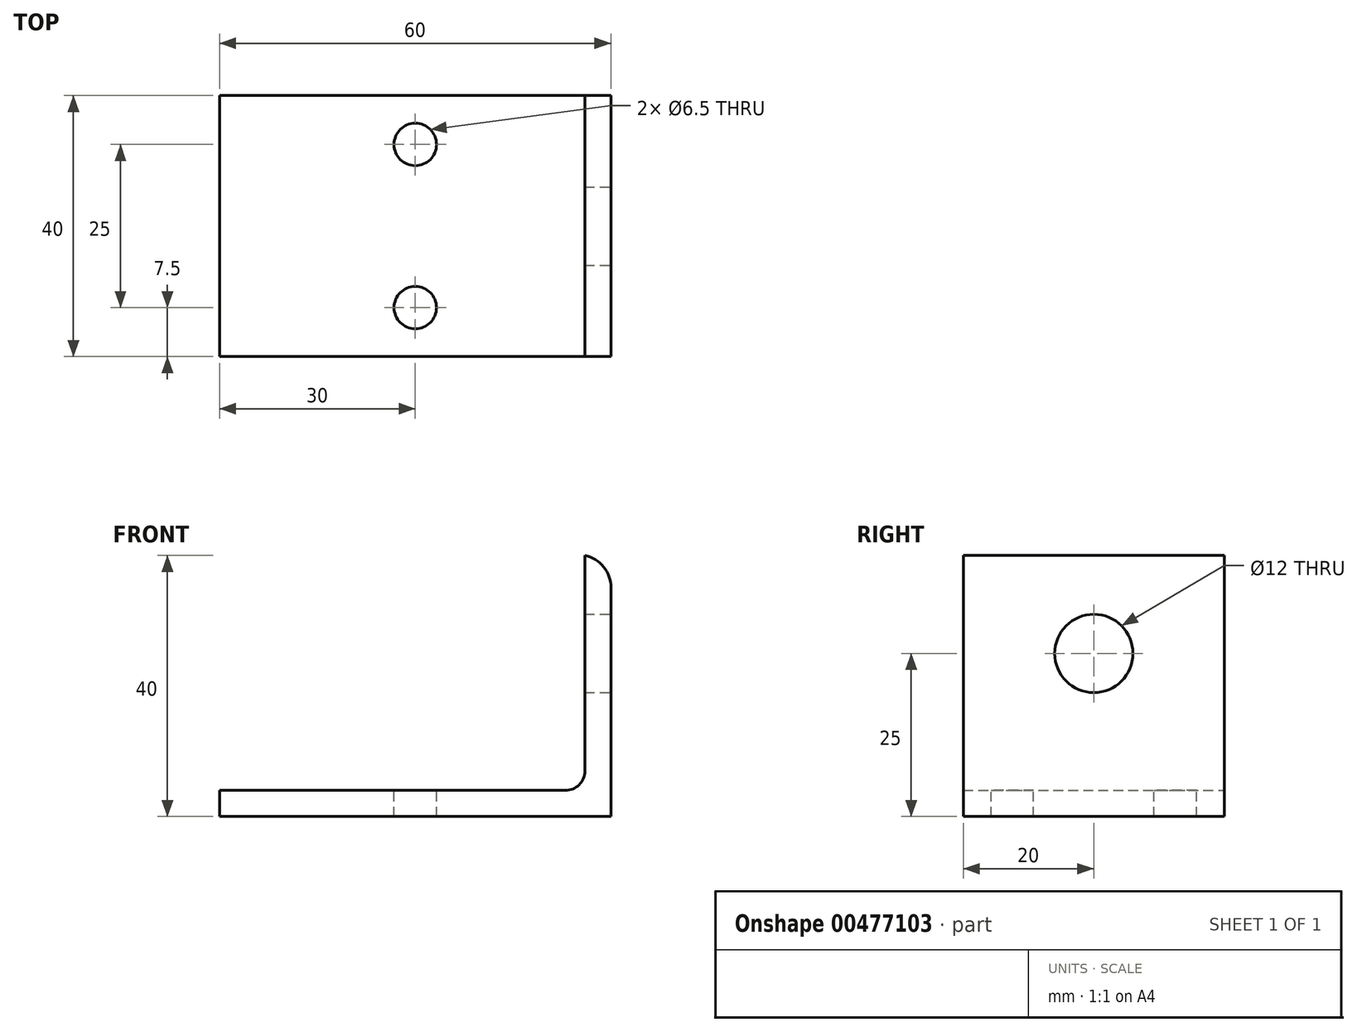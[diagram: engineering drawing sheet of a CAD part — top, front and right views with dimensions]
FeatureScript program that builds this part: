
annotation { "Feature Type Name" : "Feature", "Feature Type Description" : "" }
export const myFeature = defineFeature(function(context is Context, id is Id, definition is map)
    precondition{}
    {
        {
            var Q0;
            Q0=qCreatedBy(makeId("Front.planeOp"),FACE);
            var sketch = newSketch(context, id + "F0", { "sketchPlane" : qUnion([Q0])});
            skLineSegment(sketch, "E0.bottom", {"start": v(0, 0) * mm, "end": v(60, 0) * mm});
            skLineSegment(sketch, "E0.top", {"start": v(0, 4) * mm, "end": v(60, 4) * mm});
            skLineSegment(sketch, "E0.left", {"start": v(0, 0) * mm, "end": v(0, 4) * mm});
            skLineSegment(sketch, "E0.right", {"start": v(60, 0) * mm, "end": v(60, 4) * mm});
            skLineSegment(sketch, "E1.bottom", {"start": v(60, 0) * mm, "end": v(56, 0) * mm});
            skLineSegment(sketch, "E1.top", {"start": v(60, 40) * mm, "end": v(56, 40) * mm});
            skLineSegment(sketch, "E1.left", {"start": v(60, 0) * mm, "end": v(60, 40) * mm});
            skLineSegment(sketch, "E1.right", {"start": v(56, 0) * mm, "end": v(56, 40) * mm});
            skSolve(sketch);
        }
        {
            var Q0;
            Q0 = qSketchRegion(id + "F0", true);
            extrude(context, id + "F1", {"entities" : qUnion([Q0]), "endBound" : BoundingType.SYMMETRIC, "depth" : 40 * mm});
        }
        {
            var Q0;
            Q0=makeQuery(id+"F1.opExtrude","SWEPT_EDGE",EDGE,{"disambiguationData":[OSD([sQuery(id+"F0.wireOp",EDGE,"E1.bottom"),sQuery(id+"F0.wireOp",EDGE,"E1.left")])]});
            fillet(context, id + "F2", {"entities" : qUnion([Q0]), "radius" : 5 * mm, "tangentPropagation" : true, "allowEdgeOverflow" : false});
        }
        {
            var Q0;
            Q0=makeQuery(id+"F1.opExtrude","SWEPT_EDGE",EDGE,{"disambiguationData":[OSD([sQuery(id+"F0.wireOp",EDGE,"E0.top"),sQuery(id+"F0.wireOp",EDGE,"E1.right")])]});
            fillet(context, id + "F3", {"entities" : qUnion([Q0]), "radius" : 3 * mm, "tangentPropagation" : true, "allowEdgeOverflow" : false});
        }
        {
            var Q0;
            Q0=makeQuery(id+"F1.opExtrude","SWEPT_FACE",FACE,{"disambiguationData":[OSD([sQuery(id+"F0.wireOp",EDGE,"E1.left")])]});
            var sketch = newSketch(context, id + "F4", { "sketchPlane" : qUnion([Q0])});
            skCircle(sketch, "E2", {"center": v(0, 25) * mm, "radius": 6 * mm});
            skSolve(sketch);
        }
        {
            var Q0;
            Q0=makeQuery(id+"F4.imprint","IMPRINT",FACE,{"disambiguationData":[TD([[makeQuery(id+"F4.imprint","IMPRINT",EDGE,{"derivedFrom":sQuery(id+"F4.wireOp",EDGE,"E2")}),1.0]])]});
            extrude(context, id + "F5", {"entities" : qUnion([Q0]), "operationType" : NewBodyOperationType.REMOVE, "oppositeDirection" : true, "depth" : 4 * mm});
        }
        {
            var Q0;
            Q0=makeQuery(id+"F1.opExtrude","SWEPT_FACE",FACE,{"disambiguationData":[OSD([sQuery(id+"F0.wireOp",EDGE,"E0.top")])]});
            var sketch = newSketch(context, id + "F6", { "sketchPlane" : qUnion([Q0])});
            skCircle(sketch, "E3", {"center": v(30, -12.5) * mm, "radius": 3.25 * mm});
            skCircle(sketch, "E4", {"center": v(30, 12.5) * mm, "radius": 3.25 * mm});
            skLineSegment(sketch, "E5", {"start": v(30, -20) * mm, "end": v(30, 20) * mm});
            skSolve(sketch);
        }
        {
            var Q0;
            Q0 = qSketchRegion(id + "F6", true);
            extrude(context, id + "F7", {"entities" : qUnion([Q0]), "operationType" : NewBodyOperationType.REMOVE, "oppositeDirection" : true, "depth" : 4 * mm});
        }
    });
